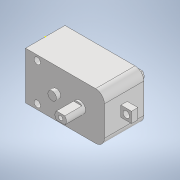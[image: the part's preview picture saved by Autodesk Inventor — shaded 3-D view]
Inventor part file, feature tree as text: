
AUTODESK INVENTOR PART (.ipt)
format: ipt  version: 2022 (Build 260153070, 153G)  size: 195,584 bytes
history: native  units: in
note: dims shown in document units (in); Inventor stores cm internally (conversion verified against a paired STEP export)
features: extrude x8, sketch x6, other x2, plane x2
ambient origin geometry x8: Origin, YZ Plane, XZ Plane, XY Plane, X Axis, Y Axis, Z Axis, Center Point
bodies: Solid1 (feature_tree)
feature tree (18):
  sketch  "Sketch1"  dims[d6=0.1575in d8=0.1181in d11=0.2165in]
  extrude  "Extrusion1"  Depth=0.1181in
  extrude  "Extrusion2"  Depth=0.3445in
  extrude  "Extrusion3"  Depth=0.5512in
  extrude  "Extrusion4"  Depth=0.1457in
  sketch  "Sketch2"  dims[d12=0.876in d13=0.3445in]
  extrude  "Extrusion5"  Depth=0.8858in TaperAngle=0.0deg
  extrude  "Extrusion6"  Depth=1.437in TaperAngle=0.0deg
  extrude  "Extrusion7"  Depth=0.1969in
  extrude  "Extrusion8"  Depth=0.1969in
  other  "Work Point1"
  sketch  "Sketch3"  dims[d16=0.5709in d17=0.5512in]
  sketch  "Sketch4"  dims[d18=1.4567in d19=0.1457in]
  sketch  "Sketch5"  dims[d20=0.7283in d21=0.0in d22=0.8858in d23=0.0in]
  sketch  "Sketch6"  dims[d24=0.8071in d25=0.0in d26=1.437in d27=0.0in d28=0.2126in d29=0.4539in d30=0.0787in d31=0.1969in d32=0.0in d33=0.0787in d34=0.1969in d35=0.0in d36=0.1181in d37=0.1969in d38=0.3346in d39=0.1969in d40=0.0in d41=0.1181in d42=0.1969in d43=0.0in]
  plane  "Work Plane1"
  plane  "Work Plane2"
  other  "Work Axis1"
